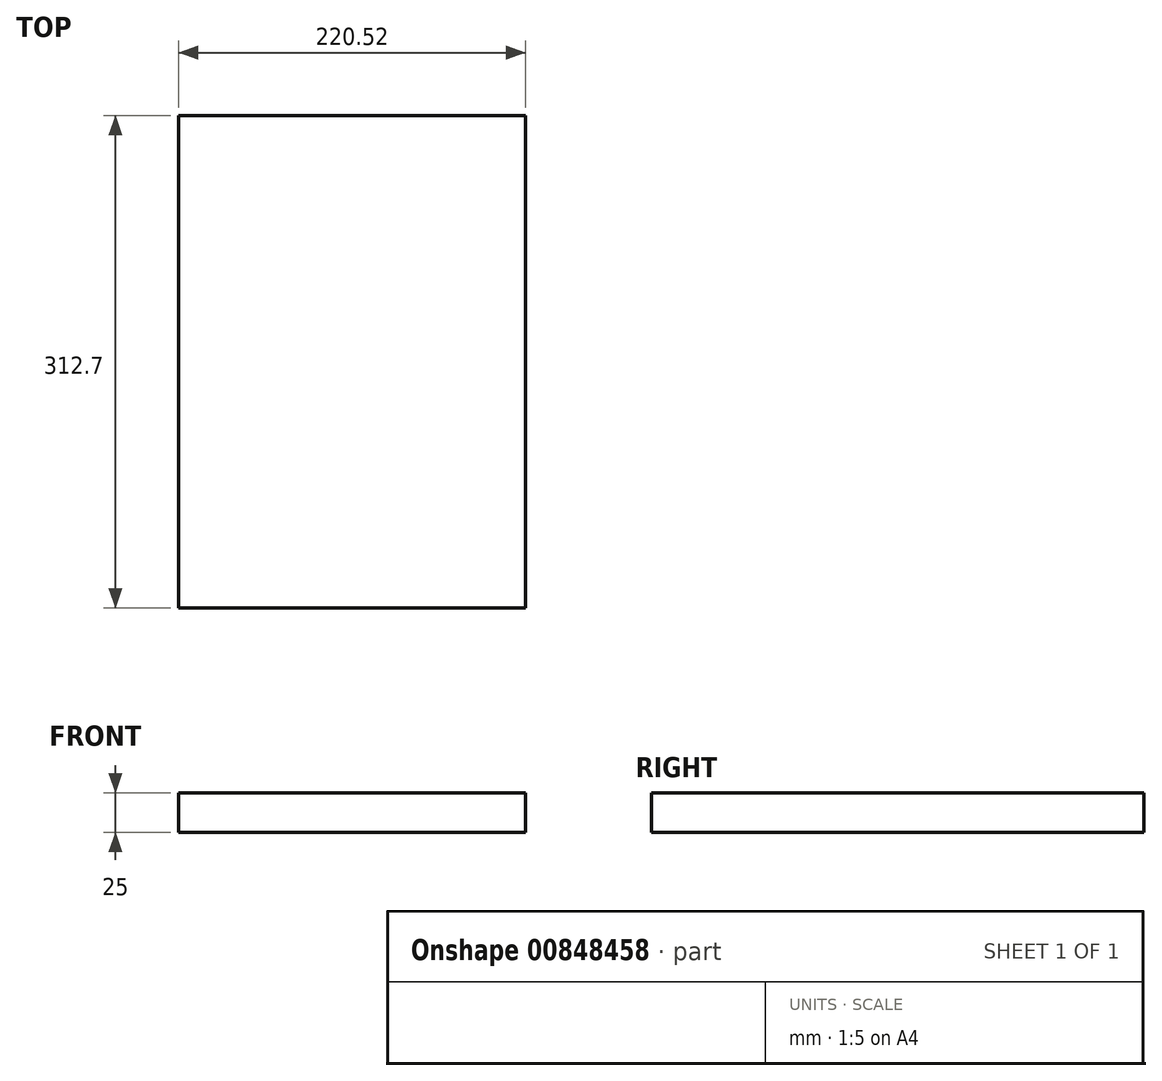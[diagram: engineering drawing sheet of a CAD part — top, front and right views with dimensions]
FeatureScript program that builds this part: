
annotation { "Feature Type Name" : "Feature", "Feature Type Description" : "" }
export const myFeature = defineFeature(function(context is Context, id is Id, definition is map)
    precondition{}
    {
        {
            var Q0;
            Q0=qCreatedBy(makeId("Top.planeOp"),FACE);
            var sketch = newSketch(context, id + "F0", { "sketchPlane" : qUnion([Q0])});
            skLineSegment(sketch, "E0.bottom", {"start": v(110.26, -156.35) * mm, "end": v(-110.26, -156.35) * mm});
            skLineSegment(sketch, "E0.top", {"start": v(110.26, 156.35) * mm, "end": v(-110.26, 156.35) * mm});
            skLineSegment(sketch, "E0.left", {"start": v(110.26, -156.35) * mm, "end": v(110.26, 156.35) * mm});
            skLineSegment(sketch, "E0.right", {"start": v(-110.26, -156.35) * mm, "end": v(-110.26, 156.35) * mm});
            skPoint(sketch, "E0.middle", {"position": v(0, 0) * mm});
            skSolve(sketch);
        }
        {
            var Q0;
            Q0=makeQuery(id+"F0.imprint","IMPRINT",FACE,{"disambiguationData":[TD([[makeQuery(id+"F0.imprint","IMPRINT",EDGE,{"derivedFrom":sQuery(id+"F0.wireOp",EDGE,"E0.bottom")}),-1.0]])]});
            extrude(context, id + "F1", {"entities" : qUnion([Q0]), "depth" : 25 * mm, "offsetDistance" : 25 * mm});
        }
    });
